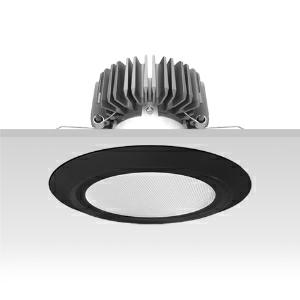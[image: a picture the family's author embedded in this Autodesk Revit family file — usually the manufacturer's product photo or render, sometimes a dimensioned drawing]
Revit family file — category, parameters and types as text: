
# Revit family: 3f_filippi_-_3f_reno_bianco_ampio_3f_filippi_-_30641_a01049_-_3f_reno_200_wh_4000-930_wide___smp_bk_a67c
name_source: partatom
category: Lighting Fixtures
units: mm (PartAtom-declared; Revit-internal decimal feet)

## family parameters
Cut with Voids When Loaded = No
Host = Face
Light Source = No
Part Type = Normal
Room Calculation Point = No
Round Connector Dimension = Use Diameter
Shared = No

## types (1)
- 3F Filippi - 3F Reno Bianco Ampio (1 x LED, 2801 lm, 43 W, 3000 K)
    Apparent Load = 43 VA
    Approval mark = CE
    CIE Flux Codes = 74 92 98 100 100
    Color Rendering = 90
    Color Temperature = 3000 K
    Control Gear = Electronic ballast
    Default Elevation = 1800 mm
    Description = ILLUMINOTECHNICAL
Luminous efficiency 100% (DLOR 100%, ULOR 0%).
Initial luminous flux of the luminaire 2801 lm.
Direct symmetric wide distribution.
Installation Interdistance Transv.D = 1.06 x hu - Long.D = 1.04 x hu.
Tabular UGR (CIE 117 - 4H-8H; S=0.25H; 70/50/20): RUG 23.1 - 23.
Beam angle: 70° - 69°.
Luminous efficacy 65 lm/W.
Lifetime (L90/B10): 30000 h. (tq+25°C)
Lifetime (L85/B10): 50000 h. (tq+25°C)
Lifetime (L70/B10): 80000 h. (tq+25°C)
Sudden decreased luminous flux after 50000 hours: 0% (C0).
Photobiological safety in compliance with IEC/TR 62778: RG1 low risk, (IEC 62471).
In compliance with IEC/EN 62722-2-1 - IEC/EN 62717 standards.

SOURCE
Compact LED module 4000/930.
Energy efficiency class (UE 2019/2020 - UE 2019/2015): F.
CIE 13.3 Colour rendering index: CRI >90 (R9 >50%).
IES TM-30 Fidelity Index: Rf = 92 Rg = 101.
CCT nominal colour temperature 3000 K.
Colour initial tolerance (MacAdam): SDCM 3.
Zhaga Book 3 compliant.

MECHANICAL
Passive heat dissipator in die-casting aluminium, oversized, for optimum thermal management of the LED module.
Parabolic element with graduated/concentric rings in white polycarbonate.
Transparent external lens with glossy and satin differentiated surfaces, with a cooling and anti-insect system in methacrylate (PMMA).
Fastening spring clips in stainless steel.
Dimensions: diameter 226 mm, height 146 mm. Weight 1.645 kg.
IP44 protection degree for exposed part, IP20 for recessed part.
Mechanical strength to impacts IK05 (0.7 joule).
Glow-wire test resistance 650°C.

ELECTRICAL
Wiring on a separate unit.
Halogen Free electronic wiring 230V-50/60Hz, power factor 0.95, THD <25%, constant output current, SELV, class II, 1 driver.
Power of the luminaire 43 W.
ENEC - CE.
SAFE FLICKER: PstLM=<1 and SVM=<0.4 (IEC TR 61547-1 and IEC TR 63158), to ensure a more comfortable and safe light.
Luminaire compliant with EN 60598-2-22 for power supply from a centralised emergency system CPSS (Central Power Supply System), not incorporated in the luminaire - high risk areas excluded. The default power and flux are 100% in AC and 100% in DC.
Ambient temperature from 0°C to +25°C.
Temperature class T6 max 85°C.
Relative humidity UR: <85%.

INSTALLATION
Pull-up recessed fitting.
False ceiling carving: 200 mm.
All accessories dedicated to this product are available on the Catalog and on our website www.3F-Filippi.com.

ACCESSORIES
A01049 - Anti-glare microprismatic SMP diffuser in methacrylate (PMMA), locked and in line with the trim, in black polycarbonate.

APPLICATIONS
Suitable product for food production plants (HACCP), IFS (Food Version 6), BRC (GSFS Food Version 7).
Environments: architectural, commercial, exhibition areas, transit areas, corridors, shops, display windows, service areas.
In false ceilings with narrow voids.

WARNING
Luminaire designed for disposal/recycling at end-of-life.
Replaceable (LED only) light source by a professional. Replaceable control gear by a professional.
    Height = 0 mm  [stored 0 ft]
    Lamp = 1 x LED
    Lamp Light Flux = 2801 lm
    Lamp Power = 43 W
    Lamp count = 1
    Length = 226 mm
    Lifetime = 50000 h
    Luminous efficacy = 65 lm/W
    Manufacturer = 3F Filippi
    ModVariant = No
    Model = 3F Filippi - 30641+A01049 - 3F Reno 200 WH 4000-930 WIDE + SMP BK
    Mounting Place = Ceiling
    Mounting Type = Recessed
    Number of Poles = 1
    OnlyDefault = Yes
    Power Factor = 1
    Product Name = 3F Filippi - 3F Reno Bianco Ampio
    Product group = recessed luminaire
    ProductGroupID = 4
    Protection Class = Protection class II
    Protection Degree = IP 20
    RLX_Detail_Level = 1
    RLX_Emergency_Light_Flux = 0 lm
    RLX_Emergency_Type = 0
    RLX_Emergency_Type_DB = No
    RlxData = <blob elided: 97577 chars, md5=9d42b504>
    Socket = socket
    Standby Power = 0 W
    System Light Flux = 2801 lm
    System Power = 43 W
    Type Comments = Product without accessories
    Type Image = 3ffilippi_3f_reno_200_bk_vs_smp.jpg
    URL = http://relux.com
    VarID = ---
    Voltage = 0 V
    Weight = 0.00 kg
    Width = 0 mm  [stored 0 ft]

note: [stored X ft] marks values corroborated as IEEE doubles in the binary element streams (Revit-internal decimal feet)

## geometry (parser evidence)
native form markers: Blend x4, Sweep x10
no freeform markers — native parametric forms only
